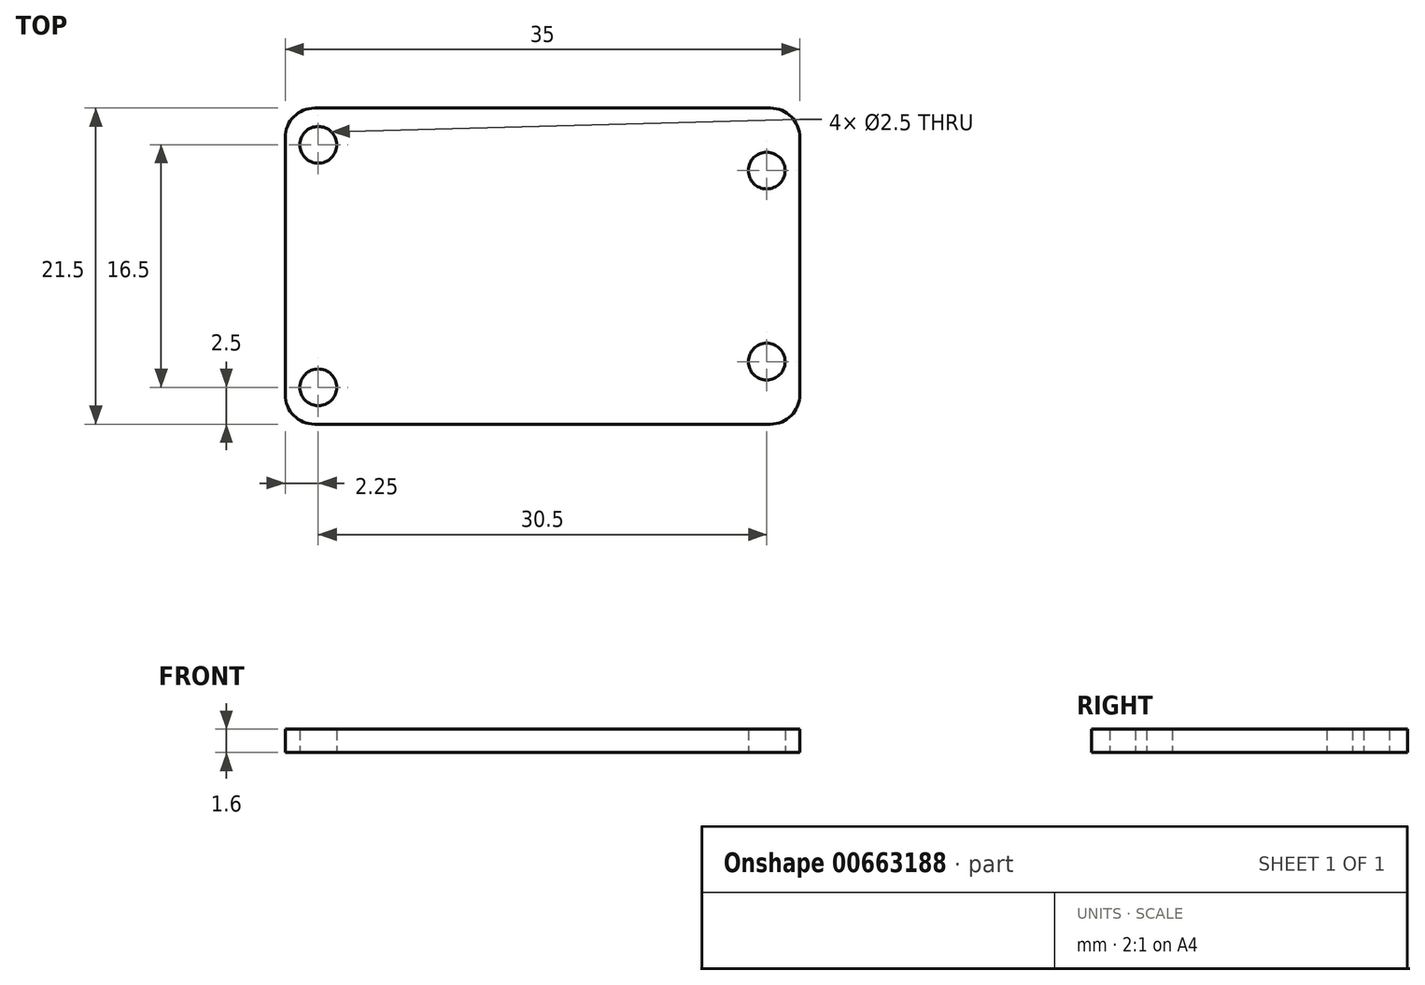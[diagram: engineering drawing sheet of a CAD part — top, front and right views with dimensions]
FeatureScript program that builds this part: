
annotation { "Feature Type Name" : "Feature", "Feature Type Description" : "" }
export const myFeature = defineFeature(function(context is Context, id is Id, definition is map)
    precondition{}
    {
        {
            var Q0;
            Q0=qCreatedBy(makeId("Top.planeOp"),FACE);
            var sketch = newSketch(context, id + "F0", { "sketchPlane" : qUnion([Q0])});
            skLineSegment(sketch, "E0.bottom", {"start": v(-17.5, 10.75) * mm, "end": v(17.5, 10.75) * mm});
            skLineSegment(sketch, "E0.top", {"start": v(-17.5, -10.75) * mm, "end": v(17.5, -10.75) * mm});
            skLineSegment(sketch, "E0.left", {"start": v(-17.5, 10.75) * mm, "end": v(-17.5, -10.75) * mm});
            skLineSegment(sketch, "E0.right", {"start": v(17.5, 10.75) * mm, "end": v(17.5, -10.75) * mm});
            skCircle(sketch, "E1", {"center": v(-15.25, 8.25) * mm, "radius": 1.25 * mm});
            skCircle(sketch, "E2.MirrorC", {"center": v(-15.25, -8.25) * mm, "radius": 1.25 * mm});
            skCircle(sketch, "E3", {"center": v(15.25, 6.5) * mm, "radius": 1.25 * mm});
            skCircle(sketch, "E4.MirrorC", {"center": v(15.25, -6.5) * mm, "radius": 1.25 * mm});
            skLineSegment(sketch, "E5", {"start": v(-15.25, 8.25) * mm, "end": v(-15.25, -8.25) * mm, "construction": true});
            skLineSegment(sketch, "E6", {"start": v(15.25, 6.5) * mm, "end": v(15.25, -6.5) * mm, "construction": true});
            skSolve(sketch);
        }
        {
            var Q0;
            Q0 = qSketchRegion(id + "F0", true);
            extrude(context, id + "F1", {"entities" : qUnion([Q0]), "depth" : 1.6 * mm, "offsetDistance" : 25 * mm});
        }
        {
            var Q0;
            Q0=makeQuery(id+"F1.opExtrude","SWEPT_EDGE",EDGE,{"disambiguationData":[OSD([sQuery(id+"F0.wireOp",EDGE,"E0.top"),sQuery(id+"F0.wireOp",EDGE,"E0.left")])]});
            var Q1;
            Q1=makeQuery(id+"F1.opExtrude","SWEPT_EDGE",EDGE,{"disambiguationData":[OSD([sQuery(id+"F0.wireOp",EDGE,"E0.top"),sQuery(id+"F0.wireOp",EDGE,"E0.right")])]});
            var Q2;
            Q2=makeQuery(id+"F1.opExtrude","SWEPT_EDGE",EDGE,{"disambiguationData":[OSD([sQuery(id+"F0.wireOp",EDGE,"E0.bottom"),sQuery(id+"F0.wireOp",EDGE,"E0.right")])]});
            var Q3;
            Q3=makeQuery(id+"F1.opExtrude","SWEPT_EDGE",EDGE,{"disambiguationData":[OSD([sQuery(id+"F0.wireOp",EDGE,"E0.bottom"),sQuery(id+"F0.wireOp",EDGE,"E0.left")])]});
            fillet(context, id + "F2", {"entities" : qUnion([Q0, Q1, Q2, Q3]), "radius" : 2 * mm, "tangentPropagation" : true, "allowEdgeOverflow" : false});
        }
    });
